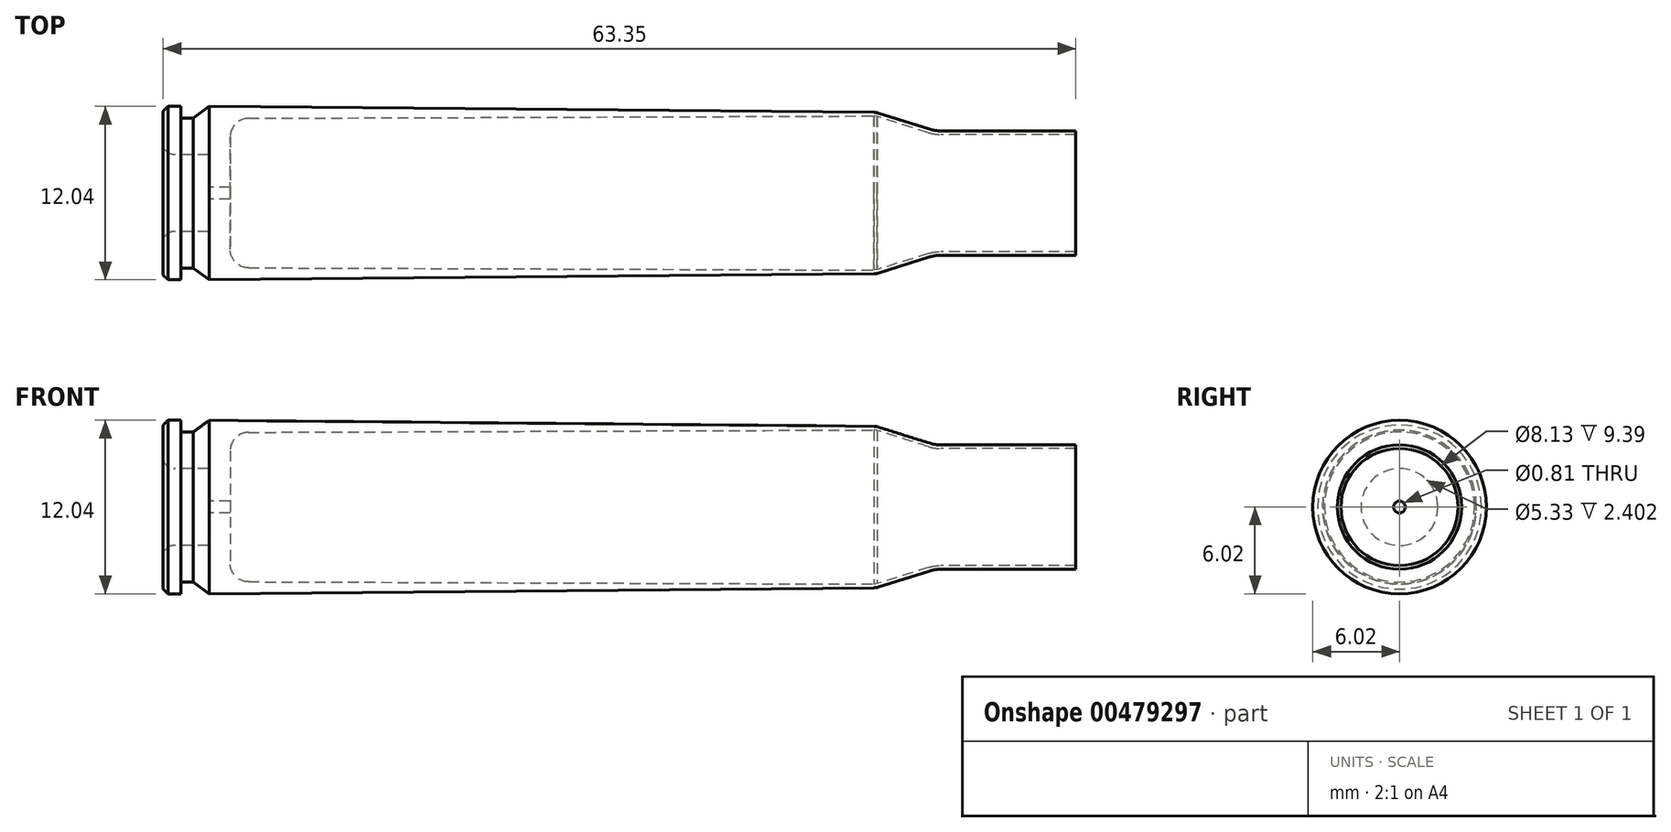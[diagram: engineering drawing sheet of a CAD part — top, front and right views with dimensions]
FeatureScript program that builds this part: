
annotation { "Feature Type Name" : "Feature", "Feature Type Description" : "" }
export const myFeature = defineFeature(function(context is Context, id is Id, definition is map)
    precondition{}
    {
        {
            var Q0;
            Q0=qCreatedBy(makeId("Front.planeOp"),FACE);
            var sketch = newSketch(context, id + "F0", { "sketchPlane" : qUnion([Q0])});
            skLineSegment(sketch, "E0", {"start": v(0, 0) * mm, "end": v(49.48, 0) * mm, "construction": true});
            skLineSegment(sketch, "E1", {"start": v(0, 0) * mm, "end": v(0, -2.67) * mm, "construction": true});
            skLineSegment(sketch, "E2", {"start": v(0, -3.43) * mm, "end": v(0, -5.69) * mm});
            skLineSegment(sketch, "E3", {"start": v(0, -5.69) * mm, "end": v(0, -6.02) * mm, "construction": true});
            skLineSegment(sketch, "E4", {"start": v(0, -6.02) * mm, "end": v(0.33, -6.02) * mm, "construction": true});
            skLineSegment(sketch, "E5", {"start": v(0, -5.69) * mm, "end": v(0.33, -6.02) * mm});
            skLineSegment(sketch, "E6", {"start": v(0.33, -6.02) * mm, "end": v(1.24, -6.02) * mm});
            skLineSegment(sketch, "E7", {"start": v(0.76, -2.67) * mm, "end": v(3.16, -2.67) * mm});
            skPoint(sketch, "E8.visualSharp", {"position": v(0, -2.67) * mm});
            skArc(sketch, "E8.filletArc", {"start": v(0.76, -2.67) * mm, "mid": v(0.22, -2.9) * mm, "end": v(0, -3.43) * mm});
            skLineSegment(sketch, "E9", {"start": v(1.24, -6.02) * mm, "end": v(1.24, -5.2) * mm});
            skLineSegment(sketch, "E10", {"start": v(1.24, -5.2) * mm, "end": v(2.08, -5.2) * mm});
            skLineSegment(sketch, "E11", {"start": v(2.08, -5.2) * mm, "end": v(2.08, -6.02) * mm, "construction": true});
            skLineSegment(sketch, "E12", {"start": v(2.08, -6.02) * mm, "end": v(3.2, -6.02) * mm, "construction": true});
            skLineSegment(sketch, "E13", {"start": v(2.08, -5.2) * mm, "end": v(3.2, -6.02) * mm});
            skLineSegment(sketch, "E14", {"start": v(3.16, -2.67) * mm, "end": v(3.16, -0.4) * mm});
            skLineSegment(sketch, "E15", {"start": v(3.16, -0.4) * mm, "end": v(4.66, -0.4) * mm});
            skLineSegment(sketch, "E16", {"start": v(49.48, 0) * mm, "end": v(49.48, -5.6) * mm, "construction": true});
            skLineSegment(sketch, "E17", {"start": v(3.2, -6.02) * mm, "end": v(49.33, -5.6) * mm});
            skLineSegment(sketch, "E18", {"start": v(49.48, 0) * mm, "end": v(53.57, 0) * mm, "construction": true});
            skLineSegment(sketch, "E19", {"start": v(53.57, 0) * mm, "end": v(53.57, -4.32) * mm, "construction": true});
            skLineSegment(sketch, "E20", {"start": v(49.62, -5.56) * mm, "end": v(53.2, -4.43) * mm});
            skPoint(sketch, "E21.visualSharp", {"position": v(49.48, -5.6) * mm});
            skArc(sketch, "E21.filletArc", {"start": v(49.33, -5.6) * mm, "mid": v(49.48, -5.59) * mm, "end": v(49.62, -5.56) * mm});
            skLineSegment(sketch, "E22", {"start": v(53.96, -4.32) * mm, "end": v(63.35, -4.32) * mm});
            skPoint(sketch, "E23.visualSharp", {"position": v(53.57, -4.32) * mm});
            skArc(sketch, "E23.filletArc", {"start": v(53.96, -4.32) * mm, "mid": v(53.57, -4.35) * mm, "end": v(53.2, -4.43) * mm});
            skLineSegment(sketch, "E24", {"start": v(4.66, -0.4) * mm, "end": v(4.66, -3.92) * mm});
            skLineSegment(sketch, "E25", {"start": v(49.33, -5.6) * mm, "end": v(49.33, -5.35) * mm, "construction": true});
            skLineSegment(sketch, "E26", {"start": v(49.33, -5.35) * mm, "end": v(5.93, -5.19) * mm});
            skPoint(sketch, "E27.visualSharp", {"position": v(4.66, -5.18) * mm});
            skArc(sketch, "E27.filletArc", {"start": v(4.66, -3.92) * mm, "mid": v(5.03, -4.81) * mm, "end": v(5.93, -5.19) * mm});
            skLineSegment(sketch, "E28.0", {"start": v(53.96, -4.06) * mm, "end": v(63.35, -4.06) * mm});
            skArc(sketch, "E28.1", {"start": v(53.96, -4.06) * mm, "mid": v(53.53, -4.1) * mm, "end": v(53.12, -4.2) * mm});
            skLineSegment(sketch, "E28.2", {"start": v(49.55, -5.31) * mm, "end": v(53.12, -4.2) * mm});
            skLineSegment(sketch, "E29", {"start": v(63.35, -4.06) * mm, "end": v(63.35, -4.32) * mm});
            skLineSegment(sketch, "E30", {"start": v(49.33, -5.35) * mm, "end": v(49.55, -5.31) * mm});
            skSolve(sketch);
        }
        {
            var Q0;
            Q0=makeQuery(id+"F0.imprint","IMPRINT",FACE,{"disambiguationData":[TD([[makeQuery(id+"F0.imprint","IMPRINT",EDGE,{"derivedFrom":sQuery(id+"F0.wireOp",EDGE,"E2")}),1.0]])]});
            var Q1;
            Q1=sQuery(id+"F0.wireOp",EDGE,"E0");
            revolve(context, id + "F1", {"entities" : qUnion([Q0]), "axis" : qUnion([Q1]), "revolveType" : RevolveType.FULL});
        }
    });
